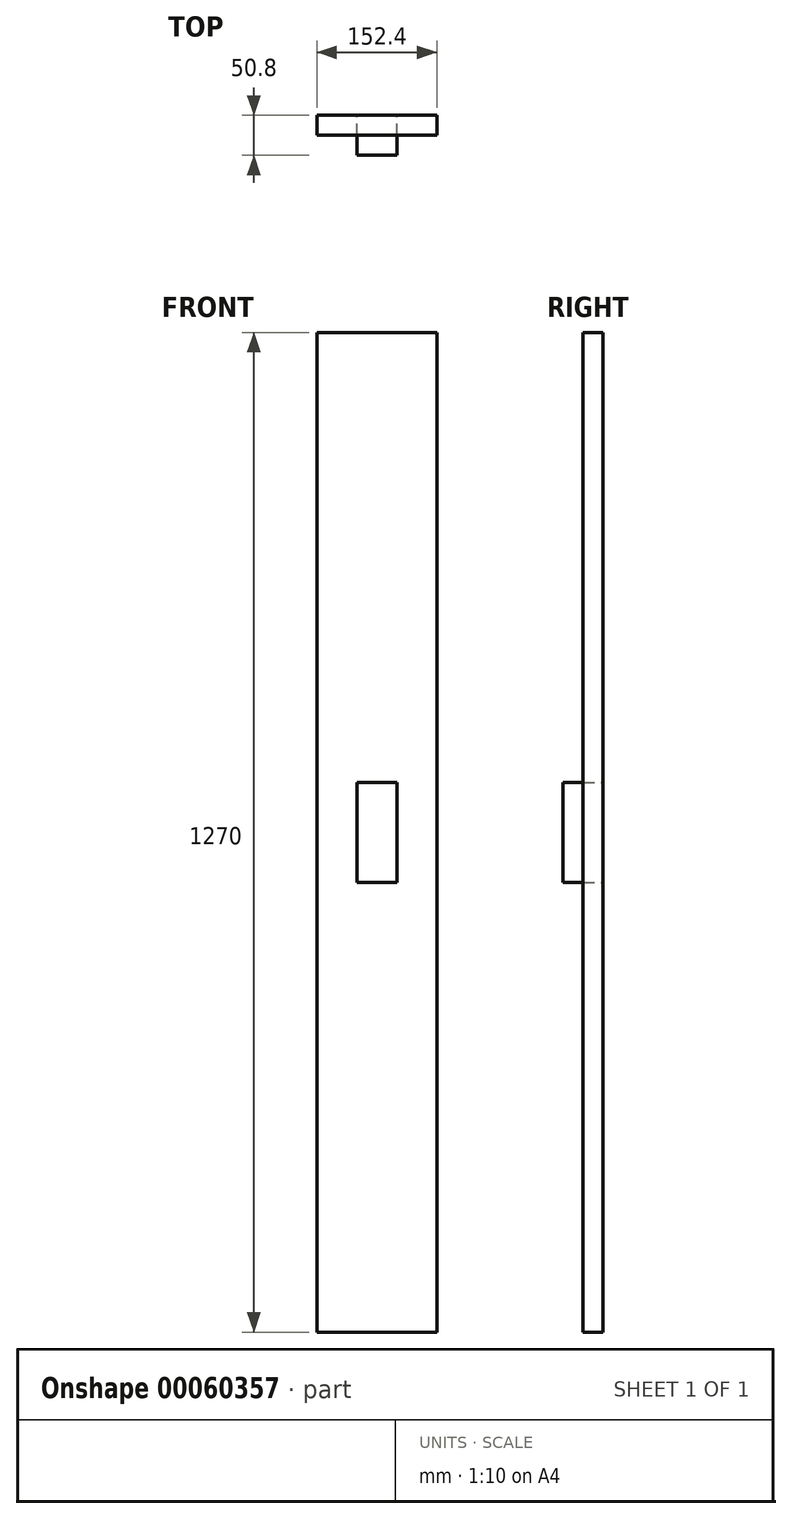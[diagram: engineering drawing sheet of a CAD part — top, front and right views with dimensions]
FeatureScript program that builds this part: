
annotation { "Feature Type Name" : "Feature", "Feature Type Description" : "" }
export const myFeature = defineFeature(function(context is Context, id is Id, definition is map)
    precondition{}
    {
        {
            var Q0;
            Q0=qCreatedBy(makeId("Front.planeOp"),FACE);
            var sketch = newSketch(context, id + "F0", { "sketchPlane" : qUnion([Q0])});
            skLineSegment(sketch, "E0.rect.bottom", {"start": v(76.2, -635) * mm, "end": v(-76.2, -635) * mm});
            skLineSegment(sketch, "E0.rect.top", {"start": v(76.2, 635) * mm, "end": v(-76.2, 635) * mm});
            skLineSegment(sketch, "E0.rect.left", {"start": v(76.2, -635) * mm, "end": v(76.2, 635) * mm});
            skLineSegment(sketch, "E0.rect.right", {"start": v(-76.2, -635) * mm, "end": v(-76.2, 635) * mm});
            skPoint(sketch, "E0.rect.middle", {"position": v(0, 0) * mm});
            skSolve(sketch);
        }
        {
            var Q0;
            Q0=makeQuery(id+"F0.imprint","IMPRINT",FACE,{"disambiguationData":[TD([[makeQuery(id+"F0.imprint","IMPRINT",EDGE,{"derivedFrom":sQuery(id+"F0.wireOp",EDGE,"E0.rect.bottom")}),-1.0]])]});
            extrude(context, id + "F1", {"entities" : qUnion([Q0]), "depth" : 25.4 * mm});
        }
        {
            var Q0;
            Q0=qCreatedBy(makeId("Front.planeOp"),FACE);
            var sketch = newSketch(context, id + "F2", { "sketchPlane" : qUnion([Q0])});
            skLineSegment(sketch, "E1.rect.bottom", {"start": v(25.4, -63.5) * mm, "end": v(-25.4, -63.5) * mm});
            skLineSegment(sketch, "E1.rect.top", {"start": v(25.4, 63.5) * mm, "end": v(-25.4, 63.5) * mm});
            skLineSegment(sketch, "E1.rect.left", {"start": v(25.4, -63.5) * mm, "end": v(25.4, 63.5) * mm});
            skLineSegment(sketch, "E1.rect.right", {"start": v(-25.4, -63.5) * mm, "end": v(-25.4, 63.5) * mm});
            skPoint(sketch, "E1.rect.middle", {"position": v(0, 0) * mm});
            skSolve(sketch);
        }
        {
            var Q0;
            Q0=makeQuery(id+"F2.imprint","IMPRINT",FACE,{"disambiguationData":[TD([[makeQuery(id+"F2.imprint","IMPRINT",EDGE,{"derivedFrom":sQuery(id+"F2.wireOp",EDGE,"E1.rect.bottom")}),-1.0]])]});
            extrude(context, id + "F3", {"entities" : qUnion([Q0]), "depth" : 50.8 * mm});
        }
    });
